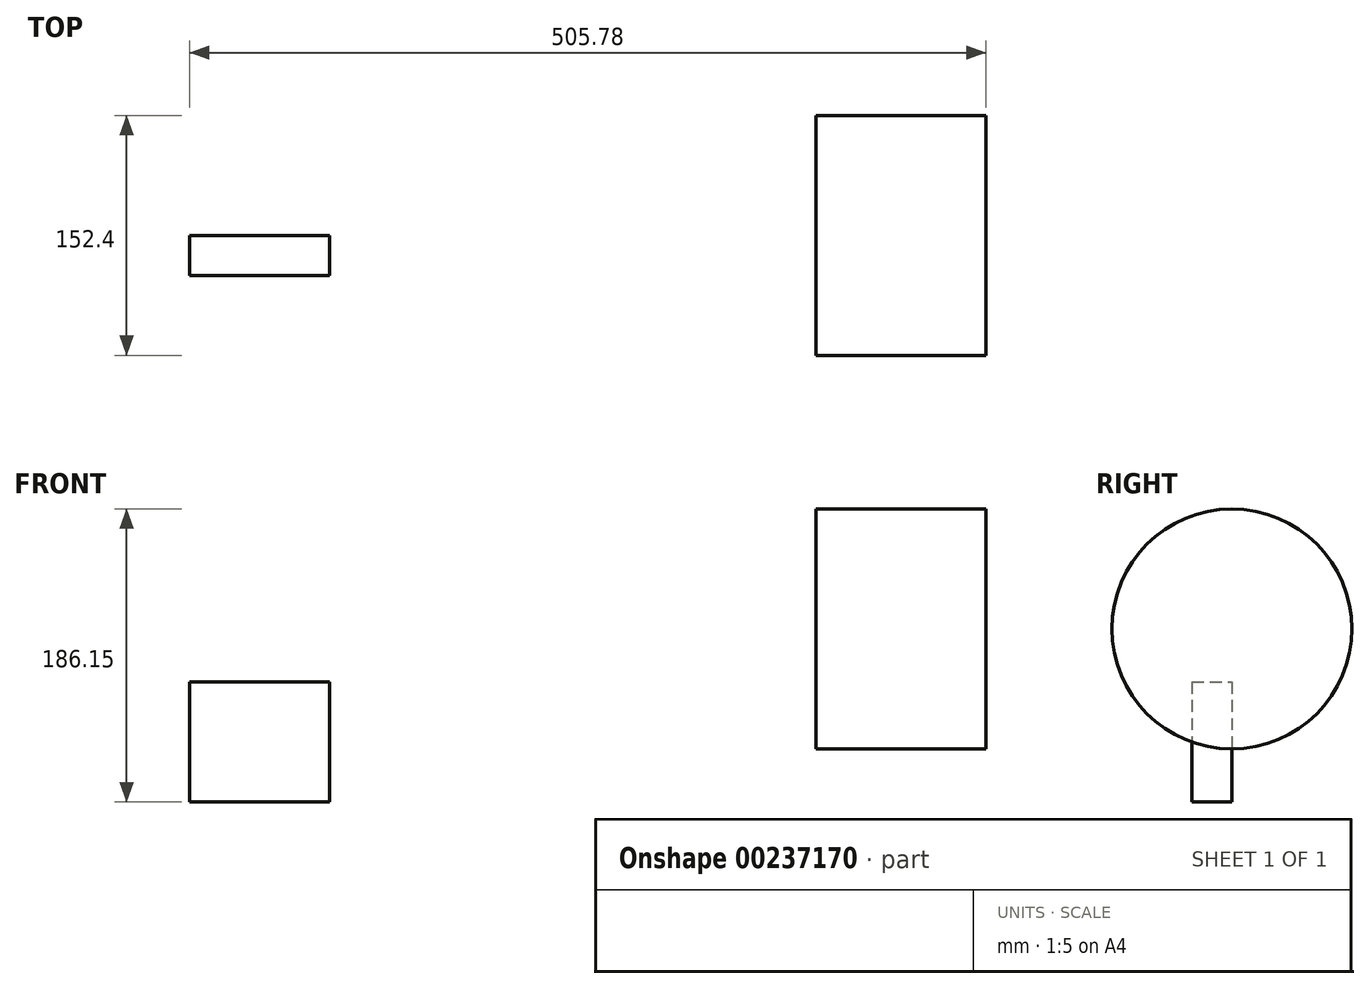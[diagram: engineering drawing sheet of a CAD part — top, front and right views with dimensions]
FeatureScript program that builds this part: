
annotation { "Feature Type Name" : "Feature", "Feature Type Description" : "" }
export const myFeature = defineFeature(function(context is Context, id is Id, definition is map)
    precondition{}
    {
        {
            var Q0;
            Q0=qCreatedBy(makeId("Right.planeOp"),FACE);
            var sketch = newSketch(context, id + "F0", { "sketchPlane" : qUnion([Q0])});
            skCircle(sketch, "E0", {"center": v(0, 0) * mm, "radius": 76.2 * mm});
            skSolve(sketch);
        }
        {
            var Q0;
            Q0 = qSketchRegion(id + "F0", true);
            extrude(context, id + "F1", {"entities" : qUnion([Q0]), "depth" : 107.95 * mm});
        }
        {
            var Q0;
            Q0=qCreatedBy(makeId("Front.planeOp"),FACE);
            var sketch = newSketch(context, id + "F2", { "sketchPlane" : qUnion([Q0])});
            skLineSegment(sketch, "E1.bottom", {"start": v(-397.83, -33.75) * mm, "end": v(-308.93, -33.75) * mm});
            skLineSegment(sketch, "E1.top", {"start": v(-397.83, -109.95) * mm, "end": v(-308.93, -109.95) * mm});
            skLineSegment(sketch, "E1.left", {"start": v(-397.83, -33.75) * mm, "end": v(-397.83, -109.95) * mm});
            skLineSegment(sketch, "E1.right", {"start": v(-308.93, -33.75) * mm, "end": v(-308.93, -109.95) * mm});
            skSolve(sketch);
        }
        {
            var Q0;
            Q0=makeQuery(id+"F2.imprint","IMPRINT",FACE,{"disambiguationData":[TD([[makeQuery(id+"F2.imprint","IMPRINT",EDGE,{"derivedFrom":sQuery(id+"F2.wireOp",EDGE,"E1.bottom")}),-1.0]])]});
            extrude(context, id + "F3", {"entities" : qUnion([Q0]), "depth" : 25.4 * mm});
        }
    });
